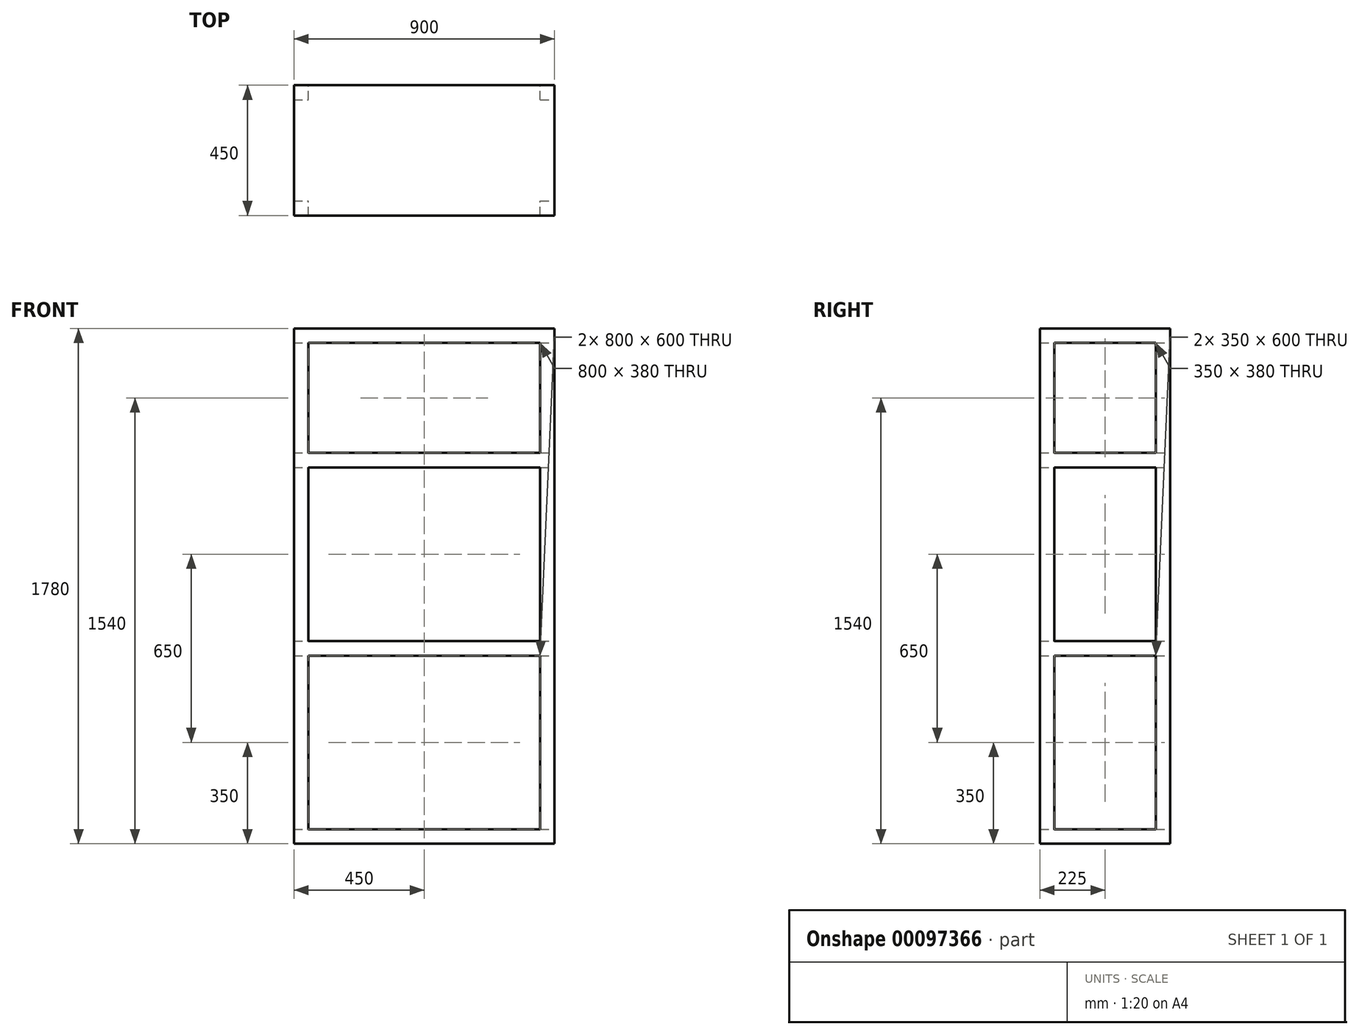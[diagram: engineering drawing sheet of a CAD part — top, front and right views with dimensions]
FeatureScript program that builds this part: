
annotation { "Feature Type Name" : "Feature", "Feature Type Description" : "" }
export const myFeature = defineFeature(function(context is Context, id is Id, definition is map)
    precondition{}
    {
        {
            var Q0;
            Q0=qCreatedBy(makeId("Front.planeOp"),FACE);
            var sketch = newSketch(context, id + "F0", { "sketchPlane" : qUnion([Q0])});
            skLineSegment(sketch, "E0.bottom", {"start": v(450, 890) * mm, "end": v(-450, 890) * mm});
            skLineSegment(sketch, "E0.top", {"start": v(450, -890) * mm, "end": v(-450, -890) * mm});
            skLineSegment(sketch, "E0.left", {"start": v(450, 890) * mm, "end": v(450, -890) * mm});
            skLineSegment(sketch, "E0.right", {"start": v(-450, 890) * mm, "end": v(-450, -890) * mm});
            skPoint(sketch, "E0.middle", {"position": v(0, 0) * mm});
            skLineSegment(sketch, "E1.bottom", {"start": v(-400, -840) * mm, "end": v(400, -840) * mm});
            skLineSegment(sketch, "E1.top", {"start": v(-400, -240) * mm, "end": v(400, -240) * mm});
            skLineSegment(sketch, "E1.left", {"start": v(-400, -840) * mm, "end": v(-400, -240) * mm});
            skLineSegment(sketch, "E1.right", {"start": v(400, -840) * mm, "end": v(400, -240) * mm});
            skLineSegment(sketch, "E2.bottom", {"start": v(-400, -190) * mm, "end": v(400, -190) * mm});
            skLineSegment(sketch, "E2.top", {"start": v(-400, 410) * mm, "end": v(400, 410) * mm});
            skLineSegment(sketch, "E2.left", {"start": v(-400, -190) * mm, "end": v(-400, 410) * mm});
            skLineSegment(sketch, "E2.right", {"start": v(400, -190) * mm, "end": v(400, 410) * mm});
            skLineSegment(sketch, "E3.bottom", {"start": v(-400, 460) * mm, "end": v(400, 460) * mm});
            skLineSegment(sketch, "E3.top", {"start": v(-400, 840) * mm, "end": v(400, 840) * mm});
            skLineSegment(sketch, "E3.left", {"start": v(-400, 460) * mm, "end": v(-400, 840) * mm});
            skLineSegment(sketch, "E3.right", {"start": v(400, 460) * mm, "end": v(400, 840) * mm});
            skLineSegment(sketch, "E4", {"start": v(-400, -840) * mm, "end": v(-450, -840) * mm, "construction": true});
            skLineSegment(sketch, "E5", {"start": v(-400, -840) * mm, "end": v(-400, -890) * mm, "construction": true});
            skLineSegment(sketch, "E6", {"start": v(-400, -240) * mm, "end": v(-400, -190) * mm, "construction": true});
            skLineSegment(sketch, "E7", {"start": v(-400, 460) * mm, "end": v(-400, 410) * mm, "construction": true});
            skLineSegment(sketch, "E8", {"start": v(-400, 840) * mm, "end": v(-450, 840) * mm, "construction": true});
            skLineSegment(sketch, "E9", {"start": v(-450, 840) * mm, "end": v(-400, 840) * mm, "construction": true});
            skLineSegment(sketch, "E10", {"start": v(-400, 840) * mm, "end": v(-400, 890) * mm, "construction": true});
            skLineSegment(sketch, "E11", {"start": v(400, -840) * mm, "end": v(450, -840) * mm, "construction": true});
            skSolve(sketch);
        }
        {
            var Q0;
            Q0=makeQuery(id+"F0.imprint","IMPRINT",FACE,{"disambiguationData":[TD([[makeQuery(id+"F0.imprint","IMPRINT",EDGE,{"derivedFrom":sQuery(id+"F0.wireOp",EDGE,"E0.bottom")}),1.0]])]});
            extrude(context, id + "F1", {"entities" : qUnion([Q0]), "depth" : 450 * mm});
        }
        {
            var Q0;
            Q0=makeQuery(id+"F1.opExtrude","SWEPT_FACE",FACE,{"disambiguationData":[OSD([sQuery(id+"F0.wireOp",EDGE,"E0.left")])]});
            var sketch = newSketch(context, id + "F2", { "sketchPlane" : qUnion([Q0])});
            skLineSegment(sketch, "E12.0", {"start": v(-450, 460) * mm, "end": v(0, 460) * mm, "construction": true});
            skLineSegment(sketch, "E13.0", {"start": v(-450, -190) * mm, "end": v(0, -190) * mm, "construction": true});
            skLineSegment(sketch, "E14.0", {"start": v(-450, 410) * mm, "end": v(0, 410) * mm, "construction": true});
            skLineSegment(sketch, "E15.0", {"start": v(-450, -240) * mm, "end": v(0, -240) * mm, "construction": true});
            skLineSegment(sketch, "E16.bottom", {"start": v(-400, 460) * mm, "end": v(-50, 460) * mm});
            skLineSegment(sketch, "E16.top", {"start": v(-400, 840) * mm, "end": v(-50, 840) * mm});
            skLineSegment(sketch, "E16.left", {"start": v(-400, 460) * mm, "end": v(-400, 840) * mm});
            skLineSegment(sketch, "E16.right", {"start": v(-50, 460) * mm, "end": v(-50, 840) * mm});
            skLineSegment(sketch, "E17.bottom", {"start": v(-400, 410) * mm, "end": v(-50, 410) * mm});
            skLineSegment(sketch, "E17.top", {"start": v(-400, -190) * mm, "end": v(-50, -190) * mm});
            skLineSegment(sketch, "E17.left", {"start": v(-400, 410) * mm, "end": v(-400, -190) * mm});
            skLineSegment(sketch, "E17.right", {"start": v(-50, 410) * mm, "end": v(-50, -190) * mm});
            skLineSegment(sketch, "E18.bottom", {"start": v(-400, -240) * mm, "end": v(-50, -240) * mm});
            skLineSegment(sketch, "E18.top", {"start": v(-400, -840) * mm, "end": v(-50, -840) * mm});
            skLineSegment(sketch, "E18.left", {"start": v(-400, -240) * mm, "end": v(-400, -840) * mm});
            skLineSegment(sketch, "E18.right", {"start": v(-50, -240) * mm, "end": v(-50, -840) * mm});
            skLineSegment(sketch, "E19", {"start": v(-400, 840) * mm, "end": v(-450, 840) * mm, "construction": true});
            skLineSegment(sketch, "E20", {"start": v(-450, 840) * mm, "end": v(-400, 840) * mm, "construction": true});
            skLineSegment(sketch, "E21", {"start": v(-400, 840) * mm, "end": v(-400, 890) * mm, "construction": true});
            skLineSegment(sketch, "E22", {"start": v(-400, 460) * mm, "end": v(-400, 410) * mm, "construction": true});
            skLineSegment(sketch, "E23", {"start": v(-400, -190) * mm, "end": v(-400, -240) * mm, "construction": true});
            skLineSegment(sketch, "E24", {"start": v(-400, -840) * mm, "end": v(-400, -890) * mm, "construction": true});
            skLineSegment(sketch, "E25", {"start": v(-50, 840) * mm, "end": v(0, 840) * mm, "construction": true});
            skSolve(sketch);
        }
        {
            var Q0;
            Q0=makeQuery(id+"F2.imprint","IMPRINT",FACE,{"disambiguationData":[TD([[makeQuery(id+"F2.imprint","IMPRINT",EDGE,{"derivedFrom":sQuery(id+"F2.wireOp",EDGE,"E16.bottom")}),1.0]])]});
            var Q1;
            Q1=makeQuery(id+"F2.imprint","IMPRINT",FACE,{"disambiguationData":[TD([[makeQuery(id+"F2.imprint","IMPRINT",EDGE,{"derivedFrom":sQuery(id+"F2.wireOp",EDGE,"E17.bottom")}),-1.0]])]});
            var Q2;
            Q2=makeQuery(id+"F2.imprint","IMPRINT",FACE,{"disambiguationData":[TD([[makeQuery(id+"F2.imprint","IMPRINT",EDGE,{"derivedFrom":sQuery(id+"F2.wireOp",EDGE,"E18.bottom")}),-1.0]])]});
            extrude(context, id + "F3", {"entities" : qUnion([Q0, Q1, Q2]), "operationType" : NewBodyOperationType.REMOVE, "endBound" : BoundingType.THROUGH_ALL, "oppositeDirection" : true, "depth" : 25 * mm});
        }
    });
